# Revit family: Font_Sofa_1200_Offecct
name_source: partatom
category: Furniture
revit_build: Autodesk Revit 2018 (Build: 20170223_1515(x64)
units: mm (PartAtom-declared; Revit-internal decimal feet)

## family parameters
Always vertical = Yes
Cut with Voids When Loaded = No
OmniClass Number = 23.40.20.14.14.14
OmniClass Title = Settees, Sofas
Room Calculation Point = No
Shared = No
Work Plane-Based = No

## types (1)
- Font sofa 1200 mm
    AssetType = Movable
    BIMObjectName = Font_Sofa_1200_Offecct
    Brand = Offecct
    Category = Sofa
    Color = Multiple
    ConvergoRefNr = 0019-2101-0006-SE
    Cost = 0 $
    Description = ont is a sofa system designed for Nationalmuseum

Nationalmuseum, which originally opened in Stockholm in 1866, was reinaugurated in 2018 after a five-year renovation.

“Font is based on a simple form with a round backrest, which gives the furniture its graphic expression and character, and indeed also inspired the name. The challenge was to achieve the right height and softness, and also a construction that enables you to use Font in a context outside of the museum”, says Matti Klenell.
    Designer = Matti Klenell
    DurationUnit = Year
    Features = Available for the United States market. Base in wood and metal. Seat and back in cold foam wrapped in flameproof fiber. Upholstered in fabric or leather. Standard leather Elmo Soft. Extra seams occur when selecting leather. Frame in metal lacquered grey RAL 7022 with black ABS glides. Test standard: EN 16139:2013 Report nr: 857070-3
    HighestSeatingHeight = 460 mm  [stored 1.50919 ft]
    IfcExportAs = IfcFurnishingElementType
    IfcExportType = SOFA
    LowestSeatingHeight = 460 mm  [stored 1.50919 ft]
    MainColor = Various
    Manufacturer = Offecct
    ManufacturerName = Offecct
    ManufacturerURL = https://www.offecct.com
    Material = Steel & fabric
    Model = Font sofa 1200mm
    ModelNumber = 10124
    Name = Font sofa
    NominalDepth = 625 mm  [stored 2.05052 ft]
    NominalHeight = 755 mm  [stored 2.47703 ft]
    NominalLength = 1200 mm  [stored 3.93701 ft]
    ProductInformation = ont is a sofa system designed for Nationalmuseum

Nationalmuseum, which originally opened in Stockholm in 1866, was reinaugurated in 2018 after a five-year renovation.

“Font is based on a simple form with a round backrest, which gives the furniture its graphic expression and character, and indeed also inspired the name. The challenge was to achieve the right height and softness, and also a construction that enables you to use Font in a context outside of the museum”, says Matti Klenell.
    SeatingHeight = 460 mm  [stored 1.50919 ft]
    Shape = Sculptured
    Size = 1200x625x755 mm
    URL = https://www.offecct.com
    Uniclass2 = Pr_40_50_12_81
    Uniclass2015Description = Sofas
    Uniclass2015Reference = Pr_40_50_12_81
    Version = 1
    VersionDate = 21/01/2021
    WarrantyDurationUnit = Year

note: [stored X ft] marks values corroborated as IEEE doubles in the binary element streams (Revit-internal decimal feet)

## geometry (parser evidence)
native form markers: Sweep x4
no freeform markers — native parametric forms only
